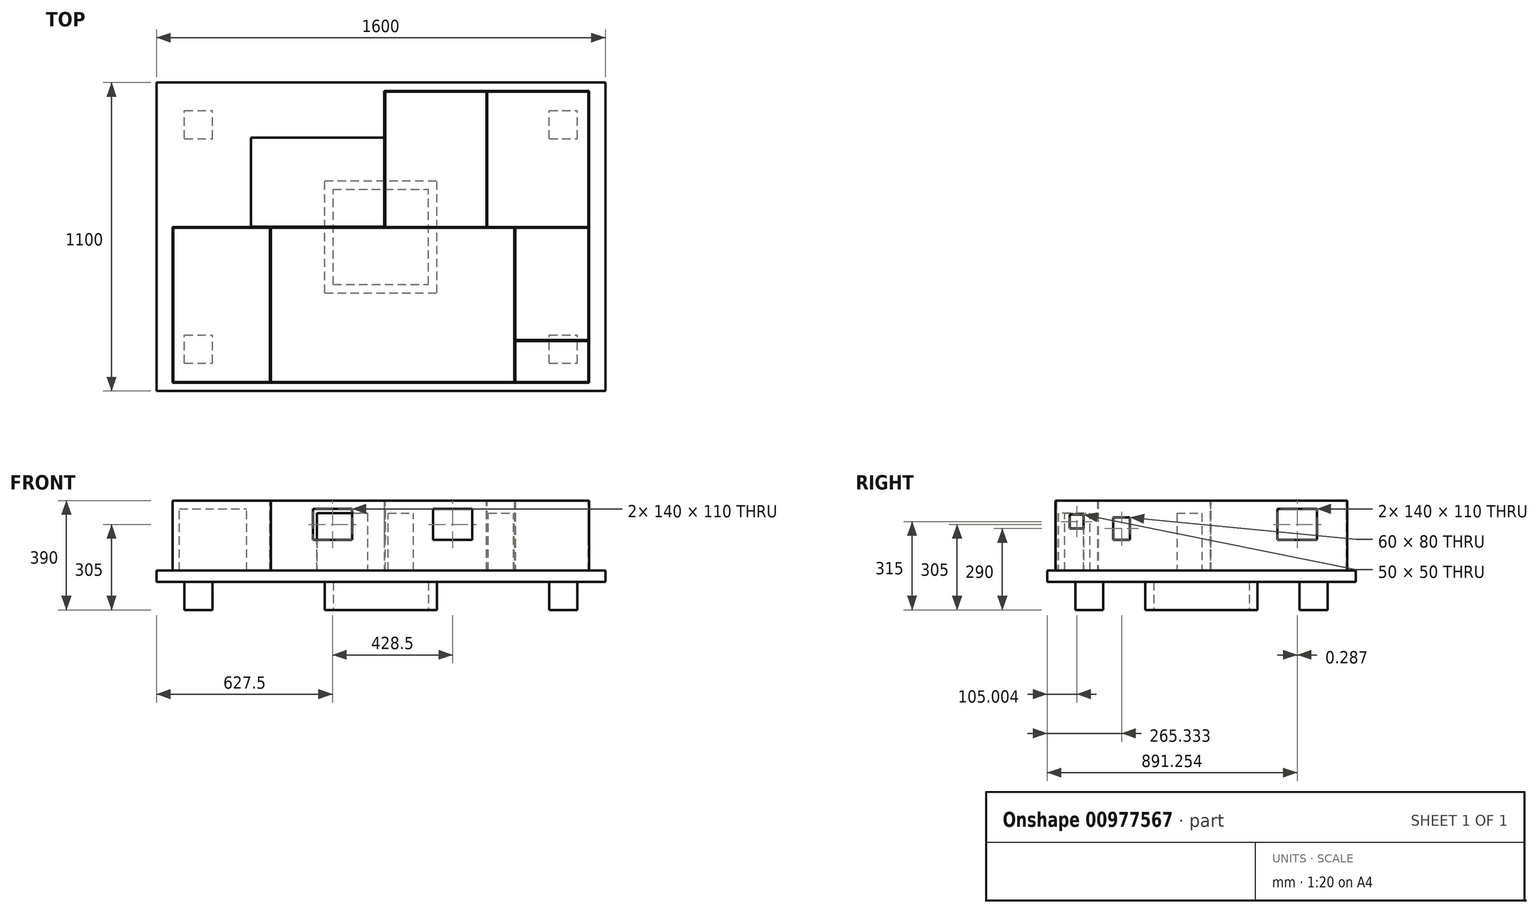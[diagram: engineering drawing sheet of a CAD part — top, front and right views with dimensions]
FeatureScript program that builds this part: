
annotation { "Feature Type Name" : "Feature", "Feature Type Description" : "" }
export const myFeature = defineFeature(function(context is Context, id is Id, definition is map)
    precondition{}
    {
        {
            var Q0;
            Q0=qCreatedBy(makeId("Top.planeOp"),FACE);
            var sketch = newSketch(context, id + "F0", { "sketchPlane" : qUnion([Q0])});
            skLineSegment(sketch, "E0.bottom", {"start": v(0, -277.73) * mm, "end": v(-330, -277.73) * mm});
            skLineSegment(sketch, "E0.top", {"start": v(0, 277.27) * mm, "end": v(-330, 277.27) * mm});
            skLineSegment(sketch, "E0.left", {"start": v(0, -277.73) * mm, "end": v(0, 277.27) * mm});
            skLineSegment(sketch, "E0.right", {"start": v(-330, -277.73) * mm, "end": v(-330, 277.27) * mm});
            skLineSegment(sketch, "E1", {"start": v(0, 277.27) * mm, "end": v(425, 277.27) * mm});
            skLineSegment(sketch, "E2", {"start": v(425, 277.27) * mm, "end": v(425, 762.27) * mm});
            skLineSegment(sketch, "E3", {"start": v(425, 762.27) * mm, "end": v(1155, 762.27) * mm});
            skLineSegment(sketch, "E4", {"start": v(1155, 762.27) * mm, "end": v(1155, -277.73) * mm});
            skLineSegment(sketch, "E5", {"start": v(1155, -277.73) * mm, "end": v(0, -277.73) * mm});
            skSolve(sketch);
        }
        {
            var Q0;
            Q0=makeQuery(id+"F0.imprint","IMPRINT",FACE,{"disambiguationData":[TD([[makeQuery(id+"F0.imprint","IMPRINT",EDGE,{"derivedFrom":sQuery(id+"F0.wireOp",EDGE,"E0.left")}),-1.0]])]});
            var Q1;
            Q1=makeQuery(id+"F0.imprint","IMPRINT",FACE,{"disambiguationData":[TD([[makeQuery(id+"F0.imprint","IMPRINT",EDGE,{"derivedFrom":sQuery(id+"F0.wireOp",EDGE,"E0.bottom")}),-1.0]])]});
            extrude(context, id + "F1", {"entities" : qUnion([Q0, Q1]), "depth" : 250 * mm, "offsetDistance" : 25 * mm});
        }
        {
            var Q0;
            Q0=makeQuery(id+"F1.opExtrude","CAP_FACE",FACE,{"disambiguationData":[OSD([sQuery(id+"F0.wireOp",EDGE,"E0.bottom"),sQuery(id+"F0.wireOp",EDGE,"E0.top"),sQuery(id+"F0.wireOp",EDGE,"E0.right"),sQuery(id+"F0.wireOp",EDGE,"E1"),sQuery(id+"F0.wireOp",EDGE,"E2"),sQuery(id+"F0.wireOp",EDGE,"E3"),sQuery(id+"F0.wireOp",EDGE,"E4"),sQuery(id+"F0.wireOp",EDGE,"E5")])],"isStart":false});
            var sketch = newSketch(context, id + "F2", { "sketchPlane" : qUnion([Q0])});
            skLineSegment(sketch, "E6", {"start": v(-327, 274.27) * mm, "end": v(428, 274.27) * mm});
            skLineSegment(sketch, "E7", {"start": v(428, 274.27) * mm, "end": v(428, 759.27) * mm});
            skLineSegment(sketch, "E8", {"start": v(428, 759.27) * mm, "end": v(1152, 759.27) * mm});
            skLineSegment(sketch, "E9", {"start": v(1152, 759.27) * mm, "end": v(1152, -274.73) * mm});
            skLineSegment(sketch, "E10", {"start": v(1152, -274.73) * mm, "end": v(-327, -274.73) * mm});
            skLineSegment(sketch, "E11", {"start": v(-327, -274.73) * mm, "end": v(-327, 274.27) * mm});
            skSolve(sketch);
        }
        {
            var Q0;
            Q0 = qSketchRegion(id + "F2", true);
            extrude(context, id + "F3", {"entities" : qUnion([Q0]), "operationType" : NewBodyOperationType.REMOVE, "oppositeDirection" : true, "depth" : 250 * mm, "offsetDistance" : 25 * mm});
        }
        {
            var Q0;
            Q0=makeQuery(id+"F1.opExtrude","CAP_FACE",FACE,{"disambiguationData":[OSD([sQuery(id+"F0.wireOp",EDGE,"E0.bottom"),sQuery(id+"F0.wireOp",EDGE,"E0.top"),sQuery(id+"F0.wireOp",EDGE,"E0.right"),sQuery(id+"F0.wireOp",EDGE,"E1"),sQuery(id+"F0.wireOp",EDGE,"E2"),sQuery(id+"F0.wireOp",EDGE,"E3"),sQuery(id+"F0.wireOp",EDGE,"E4"),sQuery(id+"F0.wireOp",EDGE,"E5")])],"isStart":true});
            var sketch = newSketch(context, id + "F4", { "sketchPlane" : qUnion([Q0])});
            skLineSegment(sketch, "E12.bottom", {"start": v(-387.5, 307.73) * mm, "end": v(1212.5, 307.73) * mm});
            skLineSegment(sketch, "E12.top", {"start": v(-387.5, -792.27) * mm, "end": v(1212.5, -792.27) * mm});
            skLineSegment(sketch, "E12.left", {"start": v(-387.5, 307.73) * mm, "end": v(-387.5, -792.27) * mm});
            skLineSegment(sketch, "E12.right", {"start": v(1212.5, 307.73) * mm, "end": v(1212.5, -792.27) * mm});
            skSolve(sketch);
        }
        {
            var Q0;
            Q0 = qSketchRegion(id + "F4", true);
            extrude(context, id + "F5", {"entities" : qUnion([Q0]), "depth" : 40 * mm, "offsetDistance" : 25 * mm});
        }
        {
            var Q0;
            Q0=makeQuery(id+"F1.opExtrude","CAP_FACE",FACE,{"disambiguationData":[OSD([sQuery(id+"F0.wireOp",EDGE,"E0.bottom"),sQuery(id+"F0.wireOp",EDGE,"E0.top"),sQuery(id+"F0.wireOp",EDGE,"E0.right"),sQuery(id+"F0.wireOp",EDGE,"E1"),sQuery(id+"F0.wireOp",EDGE,"E2"),sQuery(id+"F0.wireOp",EDGE,"E3"),sQuery(id+"F0.wireOp",EDGE,"E4"),sQuery(id+"F0.wireOp",EDGE,"E5")])],"isStart":false});
            var sketch = newSketch(context, id + "F6", { "sketchPlane" : qUnion([Q0])});
            skLineSegment(sketch, "E13.bottom", {"start": v(-330, 277.27) * mm, "end": v(20, 277.27) * mm});
            skLineSegment(sketch, "E13.top", {"start": v(-330, -277.73) * mm, "end": v(20, -277.73) * mm});
            skLineSegment(sketch, "E13.left", {"start": v(-330, 277.27) * mm, "end": v(-330, -277.73) * mm});
            skLineSegment(sketch, "E13.right", {"start": v(20, 277.27) * mm, "end": v(20, -277.73) * mm});
            skSolve(sketch);
        }
        {
            var Q0;
            Q0 = qSketchRegion(id + "F6", true);
            extrude(context, id + "F7", {"entities" : qUnion([Q0]), "oppositeDirection" : true, "depth" : 250 * mm, "offsetDistance" : 25 * mm});
        }
        {
            var Q0;
            Q0=makeQuery(id+"F7.opExtrude","CAP_FACE",FACE,{"disambiguationData":[OSD([sQuery(id+"F6.wireOp",EDGE,"E13.bottom"),sQuery(id+"F6.wireOp",EDGE,"E13.top"),sQuery(id+"F6.wireOp",EDGE,"E13.left"),sQuery(id+"F6.wireOp",EDGE,"E13.right")])],"isStart":true});
            var sketch = newSketch(context, id + "F8", { "sketchPlane" : qUnion([Q0])});
            skLineSegment(sketch, "E14.bottom", {"start": v(-327, 274.27) * mm, "end": v(17, 274.27) * mm});
            skLineSegment(sketch, "E14.top", {"start": v(-327, -274.73) * mm, "end": v(17, -274.73) * mm});
            skLineSegment(sketch, "E14.left", {"start": v(-327, 274.27) * mm, "end": v(-327, -274.73) * mm});
            skLineSegment(sketch, "E14.right", {"start": v(17, 274.27) * mm, "end": v(17, -274.73) * mm});
            skSolve(sketch);
        }
        {
            var Q0;
            Q0 = qSketchRegion(id + "F8", true);
            extrude(context, id + "F9", {"entities" : qUnion([Q0]), "operationType" : NewBodyOperationType.REMOVE, "oppositeDirection" : true, "depth" : 250 * mm, "offsetDistance" : 25 * mm});
        }
        {
            var Q0;
            Q0=makeQuery(id+"F9.boolean.opBoolean","COPY",FACE,{"derivedFrom":makeQuery(id+"F9.opExtrude","SWEPT_FACE",FACE,{"disambiguationData":[OSD([sQuery(id+"F8.wireOp",EDGE,"E14.bottom")])]})});
            var sketch = newSketch(context, id + "F10", { "sketchPlane" : qUnion([Q0])});
            skLineSegment(sketch, "E15.bottom", {"start": v(-305.43, 0) * mm, "end": v(-65.43, 0) * mm});
            skLineSegment(sketch, "E15.top", {"start": v(-305.43, 220) * mm, "end": v(-65.43, 220) * mm});
            skLineSegment(sketch, "E15.left", {"start": v(-305.43, 0) * mm, "end": v(-305.43, 220) * mm});
            skLineSegment(sketch, "E15.right", {"start": v(-65.43, 0) * mm, "end": v(-65.43, 220) * mm});
            skSolve(sketch);
        }
        {
            var Q0;
            Q0 = qSketchRegion(id + "F10", true);
            extrude(context, id + "F11", {"entities" : qUnion([Q0]), "operationType" : NewBodyOperationType.REMOVE, "oppositeDirection" : true, "depth" : 72 * mm, "offsetDistance" : 25 * mm});
        }
        {
            var Q0;
            Q0=makeQuery(id+"F7.opExtrude","SWEPT_FACE",FACE,{"disambiguationData":[OSD([sQuery(id+"F6.wireOp",EDGE,"E13.right")])]});
            var sketch = newSketch(context, id + "F12", { "sketchPlane" : qUnion([Q0])});
            skLineSegment(sketch, "E16.bottom", {"start": v(-267.73, 0) * mm, "end": v(-177.73, 0) * mm});
            skLineSegment(sketch, "E16.top", {"start": v(-267.73, 205) * mm, "end": v(-177.73, 205) * mm});
            skLineSegment(sketch, "E16.left", {"start": v(-267.73, 0) * mm, "end": v(-267.73, 205) * mm});
            skLineSegment(sketch, "E16.right", {"start": v(-177.73, 0) * mm, "end": v(-177.73, 205) * mm});
            skSolve(sketch);
        }
        {
            var Q0;
            Q0 = qSketchRegion(id + "F12", true);
            extrude(context, id + "F13", {"entities" : qUnion([Q0]), "operationType" : NewBodyOperationType.REMOVE, "oppositeDirection" : true, "depth" : 25 * mm, "offsetDistance" : 25 * mm});
        }
        {
            var Q0;
            Q0=makeQuery(id+"F1.opExtrude","CAP_FACE",FACE,{"disambiguationData":[OSD([sQuery(id+"F0.wireOp",EDGE,"E0.bottom"),sQuery(id+"F0.wireOp",EDGE,"E0.top"),sQuery(id+"F0.wireOp",EDGE,"E0.right"),sQuery(id+"F0.wireOp",EDGE,"E1"),sQuery(id+"F0.wireOp",EDGE,"E2"),sQuery(id+"F0.wireOp",EDGE,"E3"),sQuery(id+"F0.wireOp",EDGE,"E4"),sQuery(id+"F0.wireOp",EDGE,"E5")])],"isStart":false});
            var sketch = newSketch(context, id + "F14", { "sketchPlane" : qUnion([Q0])});
            skLineSegment(sketch, "E17.bottom", {"start": v(425, 762.27) * mm, "end": v(1155, 762.27) * mm});
            skLineSegment(sketch, "E17.left", {"start": v(425, 762.27) * mm, "end": v(425, 274.27) * mm});
            skLineSegment(sketch, "E17.right", {"start": v(1155, 762.27) * mm, "end": v(1155, 274.27) * mm});
            skLineSegment(sketch, "E18", {"start": v(425, 274.27) * mm, "end": v(1155, 274.27) * mm});
            skSolve(sketch);
        }
        {
            var Q0;
            Q0 = qSketchRegion(id + "F14", true);
            extrude(context, id + "F15", {"entities" : qUnion([Q0]), "operationType" : NewBodyOperationType.ADD, "oppositeDirection" : true, "depth" : 250 * mm, "offsetDistance" : 25 * mm});
        }
        {
            var Q0;
            Q0=makeQuery(id+"F15.boolean.opBoolean","MERGE",FACE,{"derivedFrom":[makeQuery(id+"F1.opExtrude","CAP_FACE",FACE,{"disambiguationData":[OSD([sQuery(id+"F0.wireOp",EDGE,"E0.bottom"),sQuery(id+"F0.wireOp",EDGE,"E0.top"),sQuery(id+"F0.wireOp",EDGE,"E0.right"),sQuery(id+"F0.wireOp",EDGE,"E1"),sQuery(id+"F0.wireOp",EDGE,"E2"),sQuery(id+"F0.wireOp",EDGE,"E3"),sQuery(id+"F0.wireOp",EDGE,"E4"),sQuery(id+"F0.wireOp",EDGE,"E5")])],"isStart":false}),makeQuery(id+"F15.opExtrude","CAP_FACE",FACE,{"disambiguationData":[OSD([sQuery(id+"F14.wireOp",EDGE,"E17.bottom"),sQuery(id+"F14.wireOp",EDGE,"E17.top"),sQuery(id+"F14.wireOp",EDGE,"E17.left"),sQuery(id+"F14.wireOp",EDGE,"E17.right")])],"isStart":true})]});
            var sketch = newSketch(context, id + "F16", { "sketchPlane" : qUnion([Q0])});
            skLineSegment(sketch, "E19.bottom", {"start": v(428, 759.27) * mm, "end": v(1152, 759.27) * mm});
            skLineSegment(sketch, "E19.left", {"start": v(428, 759.27) * mm, "end": v(428, 277.27) * mm});
            skLineSegment(sketch, "E19.right", {"start": v(1152, 759.27) * mm, "end": v(1152, 277.27) * mm});
            skLineSegment(sketch, "E20", {"start": v(428, 277.27) * mm, "end": v(1152, 277.27) * mm});
            skSolve(sketch);
        }
        {
            var Q0;
            Q0 = qSketchRegion(id + "F16", true);
            extrude(context, id + "F17", {"entities" : qUnion([Q0]), "operationType" : NewBodyOperationType.REMOVE, "oppositeDirection" : true, "depth" : 250 * mm, "offsetDistance" : 25 * mm});
        }
        {
            var Q0;
            Q0=makeQuery(id+"F15.boolean.opBoolean","MERGE",FACE,{"derivedFrom":[makeQuery(id+"F1.opExtrude","CAP_FACE",FACE,{"disambiguationData":[OSD([sQuery(id+"F0.wireOp",EDGE,"E0.bottom"),sQuery(id+"F0.wireOp",EDGE,"E0.top"),sQuery(id+"F0.wireOp",EDGE,"E0.right"),sQuery(id+"F0.wireOp",EDGE,"E1"),sQuery(id+"F0.wireOp",EDGE,"E2"),sQuery(id+"F0.wireOp",EDGE,"E3"),sQuery(id+"F0.wireOp",EDGE,"E4"),sQuery(id+"F0.wireOp",EDGE,"E5")])],"isStart":false}),makeQuery(id+"F15.opExtrude","CAP_FACE",FACE,{"disambiguationData":[OSD([sQuery(id+"F14.wireOp",EDGE,"E17.bottom"),sQuery(id+"F14.wireOp",EDGE,"E17.top"),sQuery(id+"F14.wireOp",EDGE,"E17.left"),sQuery(id+"F14.wireOp",EDGE,"E17.right")])],"isStart":true})]});
            var sketch = newSketch(context, id + "F18", { "sketchPlane" : qUnion([Q0])});
            skLineSegment(sketch, "E21.bottom", {"start": v(788.5, 762.27) * mm, "end": v(791.5, 762.27) * mm});
            skLineSegment(sketch, "E21.top", {"start": v(788.5, 274.27) * mm, "end": v(791.5, 274.27) * mm});
            skLineSegment(sketch, "E21.left", {"start": v(788.5, 762.27) * mm, "end": v(788.5, 274.27) * mm});
            skLineSegment(sketch, "E21.right", {"start": v(791.5, 762.27) * mm, "end": v(791.5, 274.27) * mm});
            skSolve(sketch);
        }
        {
            var Q0;
            Q0 = qSketchRegion(id + "F18", true);
            extrude(context, id + "F19", {"entities" : qUnion([Q0]), "oppositeDirection" : true, "depth" : 250 * mm, "offsetDistance" : 25 * mm});
        }
        {
            var Q0;
            Q0=makeQuery(id+"F5.opExtrude","CAP_FACE",FACE,{"disambiguationData":[OSD([sQuery(id+"F4.wireOp",EDGE,"E12.bottom"),sQuery(id+"F4.wireOp",EDGE,"E12.top"),sQuery(id+"F4.wireOp",EDGE,"E12.left"),sQuery(id+"F4.wireOp",EDGE,"E12.right")])],"isStart":true});
            var sketch = newSketch(context, id + "F20", { "sketchPlane" : qUnion([Q0])});
            skLineSegment(sketch, "E22.bottom", {"start": v(-50.81, 278.27) * mm, "end": v(424, 278.27) * mm});
            skLineSegment(sketch, "E22.top", {"start": v(-50.81, 596.14) * mm, "end": v(424, 596.14) * mm});
            skLineSegment(sketch, "E22.left", {"start": v(-50.81, 278.27) * mm, "end": v(-50.81, 596.14) * mm});
            skLineSegment(sketch, "E22.right", {"start": v(424, 278.27) * mm, "end": v(424, 596.14) * mm});
            skSolve(sketch);
        }
        {
            var Q0;
            Q0 = qSketchRegion(id + "F20", true);
            extrude(context, id + "F21", {"entities" : qUnion([Q0]), "operationType" : NewBodyOperationType.ADD, "depth" : 2 * mm, "offsetDistance" : 25 * mm});
        }
        {
            var Q0;
            Q0=makeQuery(id+"F5.opExtrude","CAP_FACE",FACE,{"disambiguationData":[OSD([sQuery(id+"F4.wireOp",EDGE,"E12.bottom"),sQuery(id+"F4.wireOp",EDGE,"E12.top"),sQuery(id+"F4.wireOp",EDGE,"E12.left"),sQuery(id+"F4.wireOp",EDGE,"E12.right")])],"isStart":true});
            var sketch = newSketch(context, id + "F22", { "sketchPlane" : qUnion([Q0])});
            skLineSegment(sketch, "E23", {"start": v(888.5, 274.27) * mm, "end": v(891.5, 274.27) * mm});
            skLineSegment(sketch, "E24", {"start": v(891.5, 274.27) * mm, "end": v(891.5, -125.73) * mm});
            skLineSegment(sketch, "E25", {"start": v(891.5, -125.73) * mm, "end": v(1152, -125.73) * mm});
            skLineSegment(sketch, "E26", {"start": v(1152, -125.73) * mm, "end": v(1152, -128.73) * mm});
            skLineSegment(sketch, "E27", {"start": v(1152, -128.73) * mm, "end": v(888.5, -128.73) * mm});
            skLineSegment(sketch, "E28", {"start": v(888.5, -128.73) * mm, "end": v(888.5, 274.27) * mm});
            skLineSegment(sketch, "E29", {"start": v(888.5, -128.73) * mm, "end": v(888.5, -274.73) * mm});
            skLineSegment(sketch, "E30", {"start": v(888.5, -274.73) * mm, "end": v(891.5, -274.73) * mm});
            skLineSegment(sketch, "E31", {"start": v(891.5, -274.73) * mm, "end": v(891.5, -125.73) * mm});
            skSolve(sketch);
        }
        {
            var Q0;
            Q0 = qSketchRegion(id + "F22", true);
            extrude(context, id + "F23", {"entities" : qUnion([Q0]), "depth" : 250 * mm, "offsetDistance" : 25 * mm});
        }
        {
            var Q0;
            Q0=makeQuery(id+"F23.opExtrude","SWEPT_FACE",FACE,{"disambiguationData":[OSD([sQuery(id+"F22.wireOp",EDGE,"E28"),sQuery(id+"F22.wireOp",EDGE,"E29")])]});
            var sketch = newSketch(context, id + "F24", { "sketchPlane" : qUnion([Q0])});
            skLineSegment(sketch, "E32.bottom", {"start": v(244.73, 0) * mm, "end": v(154.73, 0) * mm});
            skLineSegment(sketch, "E32.top", {"start": v(244.73, 205) * mm, "end": v(154.73, 205) * mm});
            skLineSegment(sketch, "E32.left", {"start": v(244.73, 0) * mm, "end": v(244.73, 205) * mm});
            skLineSegment(sketch, "E32.right", {"start": v(154.73, 0) * mm, "end": v(154.73, 205) * mm});
            skLineSegment(sketch, "E33.bottom", {"start": v(-244.27, 0) * mm, "end": v(-154.27, 0) * mm});
            skLineSegment(sketch, "E33.top", {"start": v(-244.27, 205) * mm, "end": v(-154.27, 205) * mm});
            skLineSegment(sketch, "E33.left", {"start": v(-244.27, 0) * mm, "end": v(-244.27, 205) * mm});
            skLineSegment(sketch, "E33.right", {"start": v(-154.27, 0) * mm, "end": v(-154.27, 205) * mm});
            skSolve(sketch);
        }
        {
            var Q0;
            Q0 = qSketchRegion(id + "F24", true);
            extrude(context, id + "F25", {"entities" : qUnion([Q0]), "operationType" : NewBodyOperationType.REMOVE, "oppositeDirection" : true, "depth" : 25 * mm, "offsetDistance" : 25 * mm});
        }
        {
            var Q0;
            Q0=makeQuery(id+"F15.boolean.opBoolean","MERGE",FACE,{"derivedFrom":[makeQuery(id+"F3.boolean.opBoolean","COPY",FACE,{"derivedFrom":makeQuery(id+"F3.opExtrude","SWEPT_FACE",FACE,{"disambiguationData":[OSD([sQuery(id+"F2.wireOp",EDGE,"E6")])]})}),makeQuery(id+"F15.opExtrude","SWEPT_FACE",FACE,{"disambiguationData":[OSD([sQuery(id+"F14.wireOp",EDGE,"E18")])]})]});
            var sketch = newSketch(context, id + "F26", { "sketchPlane" : qUnion([Q0])});
            skLineSegment(sketch, "E34.bottom", {"start": v(438, 0) * mm, "end": v(528, 0) * mm});
            skLineSegment(sketch, "E34.top", {"start": v(438, 205) * mm, "end": v(528, 205) * mm});
            skLineSegment(sketch, "E34.left", {"start": v(438, 0) * mm, "end": v(438, 205) * mm});
            skLineSegment(sketch, "E34.right", {"start": v(528, 0) * mm, "end": v(528, 205) * mm});
            skLineSegment(sketch, "E35.bottom", {"start": v(795.5, 0) * mm, "end": v(885.5, 0) * mm});
            skLineSegment(sketch, "E35.top", {"start": v(795.5, 205) * mm, "end": v(885.5, 205) * mm});
            skLineSegment(sketch, "E35.left", {"start": v(795.5, 0) * mm, "end": v(795.5, 205) * mm});
            skLineSegment(sketch, "E35.right", {"start": v(885.5, 0) * mm, "end": v(885.5, 205) * mm});
            skSolve(sketch);
        }
        {
            var Q0;
            Q0 = qSketchRegion(id + "F26", true);
            extrude(context, id + "F27", {"entities" : qUnion([Q0]), "operationType" : NewBodyOperationType.REMOVE, "oppositeDirection" : true, "depth" : 25 * mm, "offsetDistance" : 25 * mm});
        }
        {
            var Q0;
            Q0=makeQuery(id+"F1.opExtrude","SWEPT_FACE",FACE,{"disambiguationData":[OSD([sQuery(id+"F0.wireOp",EDGE,"E0.top"),sQuery(id+"F0.wireOp",EDGE,"E1")])]});
            var sketch = newSketch(context, id + "F28", { "sketchPlane" : qUnion([Q0])});
            skLineSegment(sketch, "E36.bottom", {"start": v(-365, 0) * mm, "end": v(-185, 0) * mm});
            skLineSegment(sketch, "E36.top", {"start": v(-365, 205) * mm, "end": v(-185, 205) * mm});
            skLineSegment(sketch, "E36.left", {"start": v(-365, 0) * mm, "end": v(-365, 205) * mm});
            skLineSegment(sketch, "E36.right", {"start": v(-185, 0) * mm, "end": v(-185, 205) * mm});
            skSolve(sketch);
        }
        {
            var Q0;
            Q0 = qSketchRegion(id + "F28", true);
            extrude(context, id + "F29", {"entities" : qUnion([Q0]), "operationType" : NewBodyOperationType.REMOVE, "oppositeDirection" : true, "depth" : 25 * mm, "offsetDistance" : 25 * mm});
        }
        {
            var Q0;
            Q0=makeQuery(id+"F1.opExtrude","SWEPT_FACE",FACE,{"disambiguationData":[OSD([sQuery(id+"F0.wireOp",EDGE,"E2")])]});
            var sketch = newSketch(context, id + "F30", { "sketchPlane" : qUnion([Q0])});
            skLineSegment(sketch, "E37.bottom", {"start": v(-653.81, 220) * mm, "end": v(-513.81, 220) * mm});
            skLineSegment(sketch, "E37.top", {"start": v(-653.81, 110) * mm, "end": v(-513.81, 110) * mm});
            skLineSegment(sketch, "E37.left", {"start": v(-653.81, 220) * mm, "end": v(-653.81, 110) * mm});
            skLineSegment(sketch, "E37.right", {"start": v(-513.81, 220) * mm, "end": v(-513.81, 110) * mm});
            skSolve(sketch);
        }
        {
            var Q0;
            Q0 = qSketchRegion(id + "F30", true);
            extrude(context, id + "F31", {"entities" : qUnion([Q0]), "operationType" : NewBodyOperationType.REMOVE, "oppositeDirection" : true, "depth" : 25 * mm, "offsetDistance" : 25 * mm});
        }
        {
            var Q0;
            Q0=makeQuery(id+"F1.opExtrude","SWEPT_FACE",FACE,{"disambiguationData":[OSD([sQuery(id+"F0.wireOp",EDGE,"E4")])]});
            var sketch = newSketch(context, id + "F32", { "sketchPlane" : qUnion([Q0])});
            skLineSegment(sketch, "E38.bottom", {"start": v(653.52, 110) * mm, "end": v(513.52, 110) * mm});
            skLineSegment(sketch, "E38.top", {"start": v(653.52, 220) * mm, "end": v(513.52, 220) * mm});
            skLineSegment(sketch, "E38.left", {"start": v(653.52, 110) * mm, "end": v(653.52, 220) * mm});
            skLineSegment(sketch, "E38.right", {"start": v(513.52, 110) * mm, "end": v(513.52, 220) * mm});
            skLineSegment(sketch, "E39.bottom", {"start": v(-227.73, 200) * mm, "end": v(-177.73, 200) * mm});
            skLineSegment(sketch, "E39.top", {"start": v(-227.73, 150) * mm, "end": v(-177.73, 150) * mm});
            skLineSegment(sketch, "E39.left", {"start": v(-227.73, 200) * mm, "end": v(-227.73, 150) * mm});
            skLineSegment(sketch, "E39.right", {"start": v(-177.73, 200) * mm, "end": v(-177.73, 150) * mm});
            skLineSegment(sketch, "E40.bottom", {"start": v(-72.4, 190) * mm, "end": v(-12.4, 190) * mm});
            skLineSegment(sketch, "E40.top", {"start": v(-72.4, 110) * mm, "end": v(-12.4, 110) * mm});
            skLineSegment(sketch, "E40.left", {"start": v(-72.4, 190) * mm, "end": v(-72.4, 110) * mm});
            skLineSegment(sketch, "E40.right", {"start": v(-12.4, 190) * mm, "end": v(-12.4, 110) * mm});
            skSolve(sketch);
        }
        {
            var Q0;
            Q0 = qSketchRegion(id + "F32", true);
            extrude(context, id + "F33", {"entities" : qUnion([Q0]), "operationType" : NewBodyOperationType.REMOVE, "oppositeDirection" : true, "depth" : 25 * mm, "offsetDistance" : 25 * mm});
        }
        {
            var Q0;
            Q0=makeQuery(id+"F1.opExtrude","SWEPT_FACE",FACE,{"disambiguationData":[OSD([sQuery(id+"F0.wireOp",EDGE,"E0.bottom"),sQuery(id+"F0.wireOp",EDGE,"E5")])]});
            var sketch = newSketch(context, id + "F34", { "sketchPlane" : qUnion([Q0])});
            skLineSegment(sketch, "E41.bottom", {"start": v(170, 220) * mm, "end": v(310, 220) * mm});
            skLineSegment(sketch, "E41.top", {"start": v(170, 110) * mm, "end": v(310, 110) * mm});
            skLineSegment(sketch, "E41.left", {"start": v(170, 220) * mm, "end": v(170, 110) * mm});
            skLineSegment(sketch, "E41.right", {"start": v(310, 220) * mm, "end": v(310, 110) * mm});
            skLineSegment(sketch, "E42.bottom", {"start": v(598.5, 220) * mm, "end": v(738.5, 220) * mm});
            skLineSegment(sketch, "E42.top", {"start": v(598.5, 110) * mm, "end": v(738.5, 110) * mm});
            skLineSegment(sketch, "E42.left", {"start": v(598.5, 220) * mm, "end": v(598.5, 110) * mm});
            skLineSegment(sketch, "E42.right", {"start": v(738.5, 220) * mm, "end": v(738.5, 110) * mm});
            skSolve(sketch);
        }
        {
            var Q0;
            Q0 = qSketchRegion(id + "F34", true);
            extrude(context, id + "F35", {"entities" : qUnion([Q0]), "operationType" : NewBodyOperationType.REMOVE, "oppositeDirection" : true, "depth" : 25 * mm, "offsetDistance" : 25 * mm});
        }
        {
            var Q0;
            Q0=makeQuery(id+"F5.opExtrude","CAP_FACE",FACE,{"disambiguationData":[OSD([sQuery(id+"F4.wireOp",EDGE,"E12.bottom"),sQuery(id+"F4.wireOp",EDGE,"E12.top"),sQuery(id+"F4.wireOp",EDGE,"E12.left"),sQuery(id+"F4.wireOp",EDGE,"E12.right")])],"isStart":false});
            var sketch = newSketch(context, id + "F36", { "sketchPlane" : qUnion([Q0])});
            skLineSegment(sketch, "E43.bottom", {"start": v(-287.5, 207.73) * mm, "end": v(-187.5, 207.73) * mm});
            skLineSegment(sketch, "E43.top", {"start": v(-287.5, 107.73) * mm, "end": v(-187.5, 107.73) * mm});
            skLineSegment(sketch, "E43.left", {"start": v(-287.5, 207.73) * mm, "end": v(-287.5, 107.73) * mm});
            skLineSegment(sketch, "E43.right", {"start": v(-187.5, 207.73) * mm, "end": v(-187.5, 107.73) * mm});
            skLineSegment(sketch, "E44.bottom", {"start": v(1012.5, 207.73) * mm, "end": v(1112.5, 207.73) * mm});
            skLineSegment(sketch, "E44.top", {"start": v(1012.5, 107.73) * mm, "end": v(1112.5, 107.73) * mm});
            skLineSegment(sketch, "E44.left", {"start": v(1012.5, 207.73) * mm, "end": v(1012.5, 107.73) * mm});
            skLineSegment(sketch, "E44.right", {"start": v(1112.5, 207.73) * mm, "end": v(1112.5, 107.73) * mm});
            skLineSegment(sketch, "E45.bottom", {"start": v(1012.5, -592.27) * mm, "end": v(1112.5, -592.27) * mm});
            skLineSegment(sketch, "E45.top", {"start": v(1012.5, -692.27) * mm, "end": v(1112.5, -692.27) * mm});
            skLineSegment(sketch, "E45.left", {"start": v(1012.5, -592.27) * mm, "end": v(1012.5, -692.27) * mm});
            skLineSegment(sketch, "E45.right", {"start": v(1112.5, -592.27) * mm, "end": v(1112.5, -692.27) * mm});
            skLineSegment(sketch, "E46.bottom", {"start": v(-287.5, -592.27) * mm, "end": v(-187.5, -592.27) * mm});
            skLineSegment(sketch, "E46.top", {"start": v(-287.5, -692.27) * mm, "end": v(-187.5, -692.27) * mm});
            skLineSegment(sketch, "E46.left", {"start": v(-287.5, -592.27) * mm, "end": v(-287.5, -692.27) * mm});
            skLineSegment(sketch, "E46.right", {"start": v(-187.5, -592.27) * mm, "end": v(-187.5, -692.27) * mm});
            skSolve(sketch);
        }
        {
            var Q0;
            Q0 = qSketchRegion(id + "F36", true);
            extrude(context, id + "F37", {"entities" : qUnion([Q0]), "operationType" : NewBodyOperationType.ADD, "depth" : 100 * mm, "offsetDistance" : 25 * mm});
        }
        {
            var Q0;
            Q0=makeQuery(id+"F5.opExtrude","CAP_FACE",FACE,{"disambiguationData":[OSD([sQuery(id+"F4.wireOp",EDGE,"E12.bottom"),sQuery(id+"F4.wireOp",EDGE,"E12.top"),sQuery(id+"F4.wireOp",EDGE,"E12.left"),sQuery(id+"F4.wireOp",EDGE,"E12.right")])],"isStart":false});
            var sketch = newSketch(context, id + "F38", { "sketchPlane" : qUnion([Q0])});
            skLineSegment(sketch, "E47.bottom", {"start": v(212.5, -42.27) * mm, "end": v(612.5, -42.27) * mm});
            skLineSegment(sketch, "E47.top", {"start": v(212.5, -442.27) * mm, "end": v(612.5, -442.27) * mm});
            skLineSegment(sketch, "E47.left", {"start": v(212.5, -42.27) * mm, "end": v(212.5, -442.27) * mm});
            skLineSegment(sketch, "E47.right", {"start": v(612.5, -42.27) * mm, "end": v(612.5, -442.27) * mm});
            skSolve(sketch);
        }
        {
            var Q0;
            Q0 = qSketchRegion(id + "F38", true);
            extrude(context, id + "F39", {"entities" : qUnion([Q0]), "operationType" : NewBodyOperationType.ADD, "depth" : 100 * mm, "offsetDistance" : 25 * mm});
        }
        {
            var Q0;
            Q0=makeQuery(id+"F39.opExtrude","CAP_FACE",FACE,{"disambiguationData":[OSD([sQuery(id+"F38.wireOp",EDGE,"E47.bottom"),sQuery(id+"F38.wireOp",EDGE,"E47.top"),sQuery(id+"F38.wireOp",EDGE,"E47.left"),sQuery(id+"F38.wireOp",EDGE,"E47.right")])],"isStart":false});
            var sketch = newSketch(context, id + "F40", { "sketchPlane" : qUnion([Q0])});
            skLineSegment(sketch, "E48.bottom", {"start": v(242.5, -72.27) * mm, "end": v(582.5, -72.27) * mm});
            skLineSegment(sketch, "E48.top", {"start": v(242.5, -412.27) * mm, "end": v(582.5, -412.27) * mm});
            skLineSegment(sketch, "E48.left", {"start": v(242.5, -72.27) * mm, "end": v(242.5, -412.27) * mm});
            skLineSegment(sketch, "E48.right", {"start": v(582.5, -72.27) * mm, "end": v(582.5, -412.27) * mm});
            skSolve(sketch);
        }
        {
            var Q0;
            Q0 = qSketchRegion(id + "F40", true);
            extrude(context, id + "F41", {"entities" : qUnion([Q0]), "operationType" : NewBodyOperationType.REMOVE, "oppositeDirection" : true, "depth" : 100 * mm, "offsetDistance" : 25 * mm});
        }
    });
